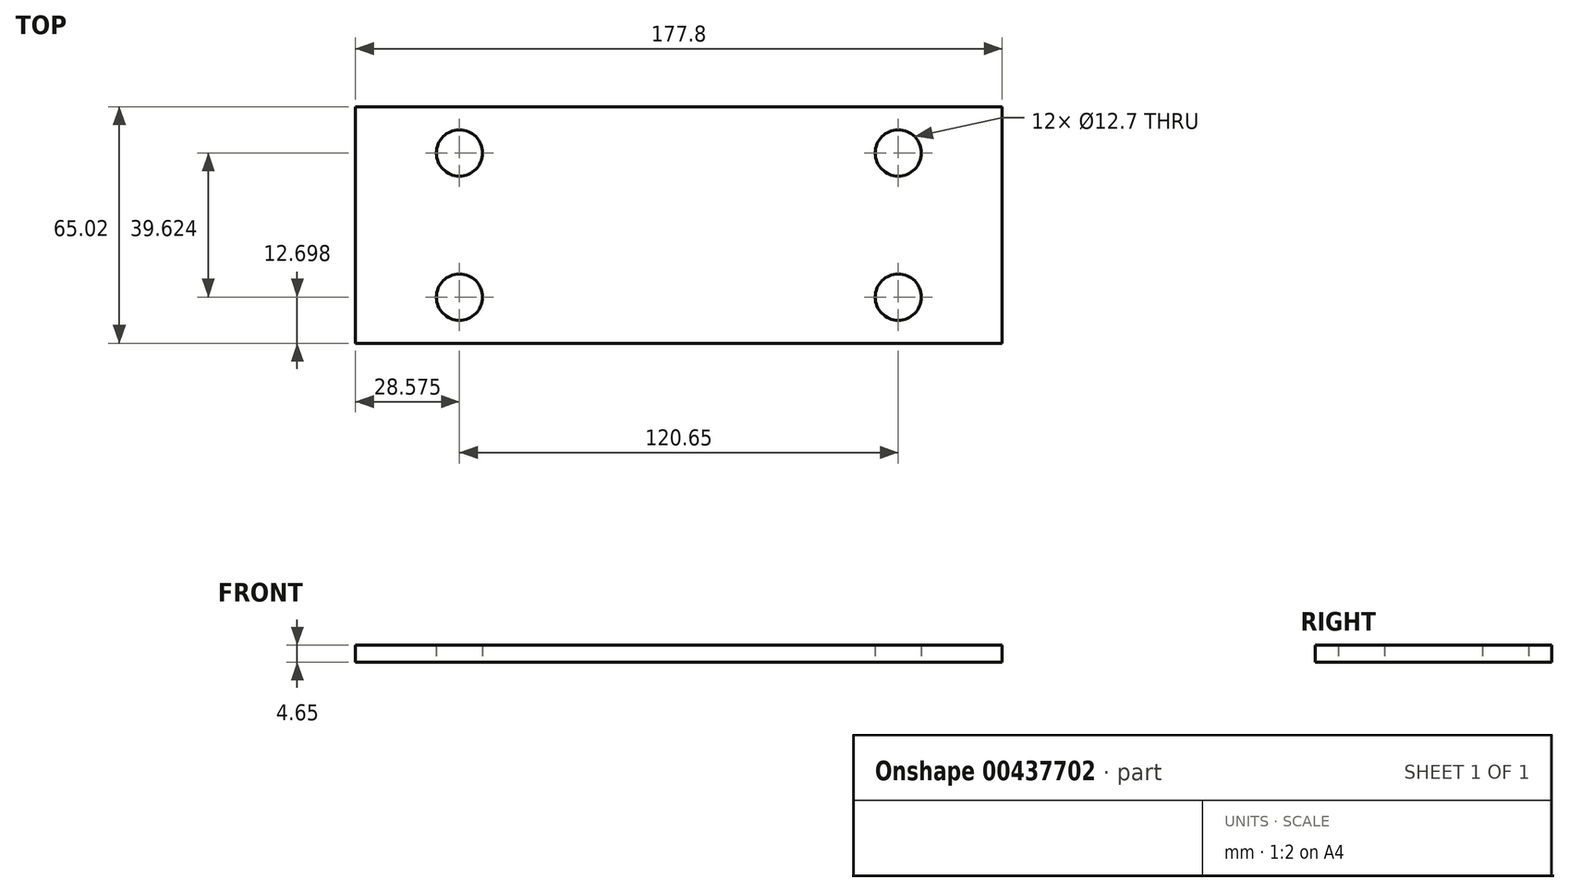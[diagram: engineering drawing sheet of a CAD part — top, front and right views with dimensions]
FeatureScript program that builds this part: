
annotation { "Feature Type Name" : "Feature", "Feature Type Description" : "" }
export const myFeature = defineFeature(function(context is Context, id is Id, definition is map)
    precondition{}
    {
        {
            var Q0;
            Q0=qCreatedBy(makeId("Top.planeOp"),FACE);
            var sketch = newSketch(context, id + "F0", { "sketchPlane" : qUnion([Q0])});
            skLineSegment(sketch, "E0.bottom", {"start": v(-88.9, 32.51) * mm, "end": v(88.9, 32.51) * mm});
            skLineSegment(sketch, "E0.top", {"start": v(-88.9, -32.51) * mm, "end": v(88.9, -32.51) * mm});
            skLineSegment(sketch, "E0.left", {"start": v(-88.9, 32.51) * mm, "end": v(-88.9, -32.51) * mm});
            skLineSegment(sketch, "E0.right", {"start": v(88.9, 32.51) * mm, "end": v(88.9, -32.51) * mm});
            skPoint(sketch, "E0.middle", {"position": v(0, 0) * mm});
            skLineSegment(sketch, "E1.bottom", {"start": v(-60.33, 19.81) * mm, "end": v(60.33, 19.81) * mm, "construction": true});
            skLineSegment(sketch, "E1.top", {"start": v(-60.33, -19.81) * mm, "end": v(60.33, -19.81) * mm, "construction": true});
            skLineSegment(sketch, "E1.left", {"start": v(-60.32, 19.81) * mm, "end": v(-60.33, -19.81) * mm, "construction": true});
            skLineSegment(sketch, "E1.right", {"start": v(60.33, 19.81) * mm, "end": v(60.33, -19.81) * mm, "construction": true});
            skCircle(sketch, "E2", {"center": v(-60.33, 19.81) * mm, "radius": 6.35 * mm});
            skCircle(sketch, "E3", {"center": v(60.33, 19.81) * mm, "radius": 6.35 * mm});
            skCircle(sketch, "E4", {"center": v(-60.33, -19.81) * mm, "radius": 6.35 * mm});
            skCircle(sketch, "E5", {"center": v(60.33, -19.81) * mm, "radius": 6.35 * mm});
            skSolve(sketch);
        }
        {
            var Q0;
            Q0 = qSketchRegion(id + "F0", true);
            extrude(context, id + "F1", {"entities" : qUnion([Q0]), "depth" : 4.65 * mm});
        }
    });
